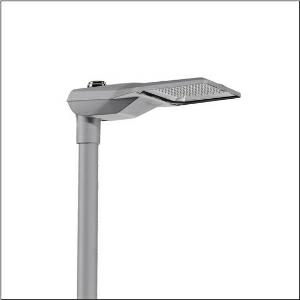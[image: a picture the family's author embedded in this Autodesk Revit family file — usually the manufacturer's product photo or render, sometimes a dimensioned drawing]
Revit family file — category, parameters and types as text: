
# Revit family: streetlight_sl_21_midi___p0_8a_5xe7u27n08mb_4af6
name_source: partatom
category: Lighting Fixtures
units: mm (PartAtom-declared; Revit-internal decimal feet)

## family parameters
Cut with Voids When Loaded = No
Host = Face
Light Source = No
Part Type = Normal
Room Calculation Point = No
Round Connector Dimension = Use Diameter
Shared = No

## types (1)
- --- (1 x LED, 15120 lm, 134.3 W, 2200K)
    Apparent Load = 134 VA
    CIE Flux Codes = 33 69 96 100 100
    Color Rendering = 70
    Color Temperature = 2200K
    Default Elevation = 1800 mm
    Description = Streetlight SL 21 midi, mast luminaire, primary light control with lens, of PMMA, primary optical cover: cover, of toughened safety glass, transparent, light distribution: P0.8a, light emission: direct distribution, primary light characteristic: asymmetric, installation type: side-entry, LED, 3G 2.5mm², High Power LED, rated luminous flux: 15.120lm, luminous efficacy: 113lm/W, light colour: 722, colour temperature: 2200K, control gear: NEMA (7pin), control: flexible luminous flux parameterisation, time-dependent luminous flux control, constant luminous flux control, pre-setting: linear dimming characteristic, overheat protection, mains connection: 220..240V, AC, 50/60Hz, connection cable pre-assembled, cable length: 12,5m, wiring characteristics: H05VV-F, start of lifetime: 134W, end of service life: 141W, reduction: 60W, luminaire housing, of diecast aluminium (EN AC-44300), powder-coated, SITECO metallic grey (DB 702S), corrosivity category C5 high according to DIN EN ISO 12944, multi-level sealing system, sealing non-destructively replaceable, inclination adjustable: 0°, 5°, 10°, 15°, length: 644mm, width: 335mm, height: 110mm, spigot size: 42mm (side-entry), mounting height: 4..8m, protection rating (complete): IP66, insulation class (complete): insulation class I (protective earthing), certification: CE, ENEC, ENEC+, VDE, impact resistance: IK10, permissible operating ambient temperature for outdoor applications: -40..+50°C, standard-compliant lighting for roads and squares, packaging unit: 1 piece

Light Distribution: P0.8a
    Height = 111 mm
    Lamp = 1 x LED
    Lamp Light Flux = 15120 lm
    Lamp Power = 134.3 W
    Lamp count = 1
    Length = 644 mm
    Luminous efficacy = 113 lm/W
    Manufacturer = Siteco
    ModVariant = No
    Model = 5XE7U27N08MB
    Number of Poles = 1
    OnlyDefault = Yes
    Power Factor = 1
    Product Name = Streetlight SL 21 midi | P0.8a
    Product group = mast luminaire | pylon top
    ProductGroupID = 6100
    Protection Class = Protection class I
    Protection Degree = IP 66
    RLX_Detail_Level = 1
    RLX_Emergency_Light_Flux = 0 lm
    RLX_Emergency_Type = 0
    RLX_Emergency_Type_DB = No
    RlxData = <blob elided: 89981 chars, md5=ec00fe08>
    Socket = socket
    Standby Power = 0 W
    System Light Flux = 15119 lm
    System Power = 134 W
    Type Comments = factory setting: luminous flux: 100 % | dim-lin: 254 | 687 mA
    Type Image = l_1294377.jpg
    URL = http://relux.com
    VarID = @adj_081049
    Voltage = 0 V
    Weight = 0.00 kg
    Width = 336 mm

## geometry (parser evidence)
native form markers: Blend x4, Sweep x11
no freeform markers — native parametric forms only
